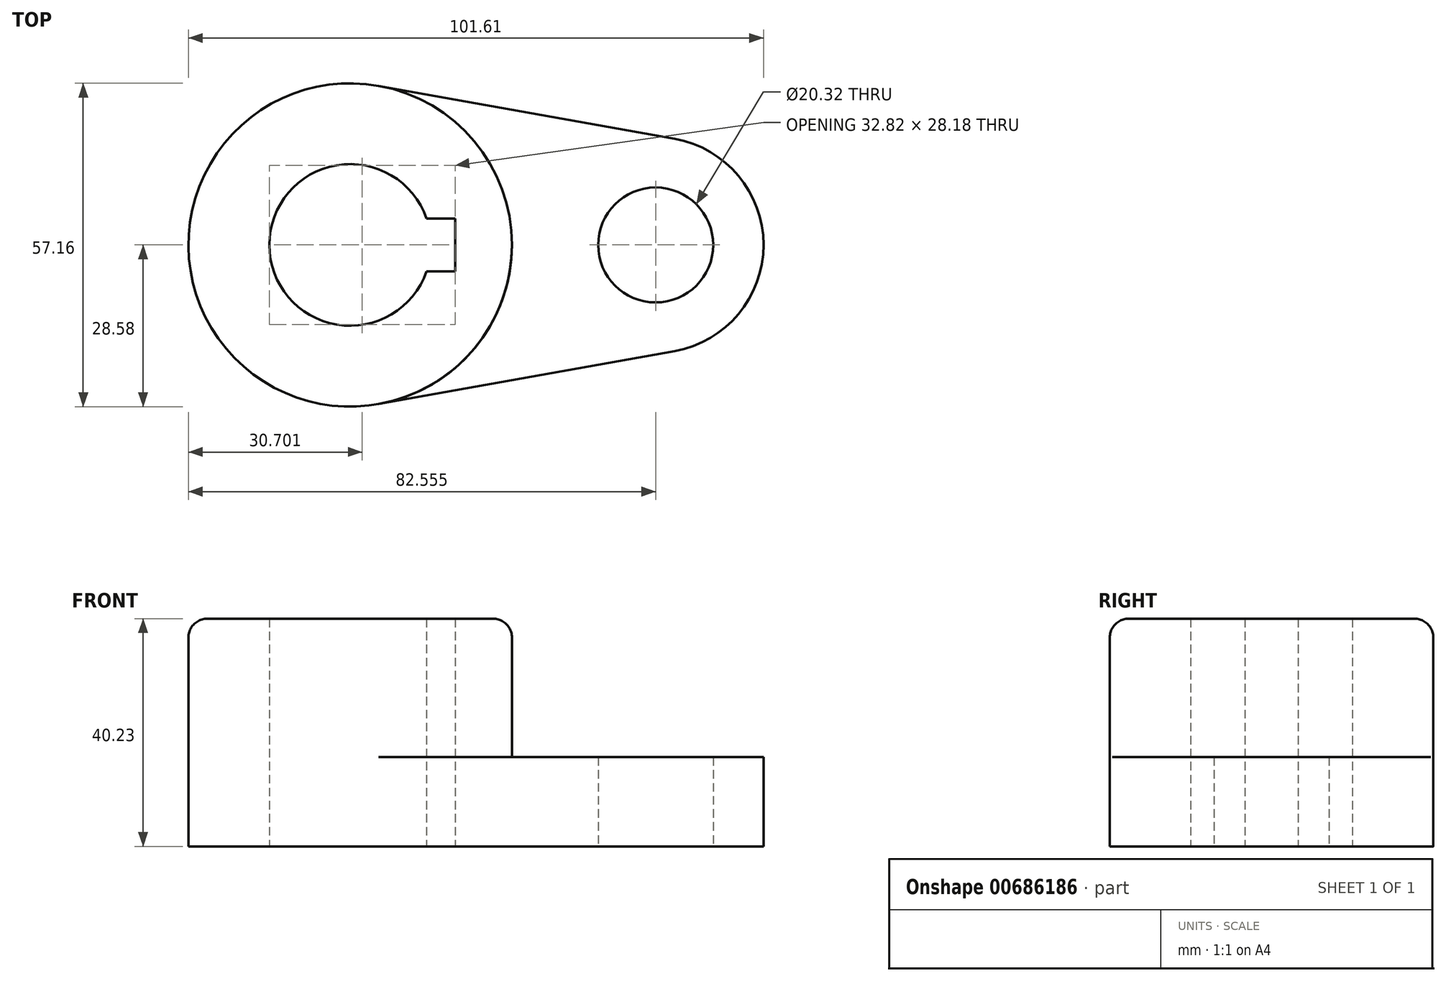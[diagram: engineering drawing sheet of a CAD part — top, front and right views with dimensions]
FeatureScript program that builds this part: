
annotation { "Feature Type Name" : "Feature", "Feature Type Description" : "" }
export const myFeature = defineFeature(function(context is Context, id is Id, definition is map)
    precondition{}
    {
        {
            var Q0;
            Q0=qCreatedBy(makeId("Top.planeOp"),FACE);
            var sketch = newSketch(context, id + "F0", { "sketchPlane" : qUnion([Q0])});
            skCircle(sketch, "E0", {"center": v(0, 0) * mm, "radius": 28.58 * mm});
            skPoint(sketch, "E1.orphan", {"position": v(-12.82, 3.46) * mm});
            skPoint(sketch, "E2.orphan", {"position": v(-12.82, -3.46) * mm});
            skCircle(sketch, "E3", {"center": v(53.98, 0) * mm, "radius": 19.05 * mm});
            skArc(sketch, "E4", {"start": v(13.5, 4.69) * mm, "mid": v(-14.29, 0) * mm, "end": v(13.5, -4.69) * mm});
            skPoint(sketch, "E5.left.end.orphan", {"position": v(12.82, 3.46) * mm});
            skPoint(sketch, "E5.bottom.start.orphan", {"position": v(12.82, -3.46) * mm});
            skLineSegment(sketch, "E6.bottom", {"start": v(13.5, 4.69) * mm, "end": v(18.53, 4.69) * mm});
            skLineSegment(sketch, "E6.top", {"start": v(13.5, -4.69) * mm, "end": v(18.53, -4.69) * mm});
            skLineSegment(sketch, "E6.right", {"start": v(18.53, 4.69) * mm, "end": v(18.53, -4.69) * mm});
            skPoint(sketch, "E6.left.start.orphan", {"position": v(-18.53, 4.69) * mm});
            skPoint(sketch, "E7.orphan", {"position": v(-18.53, -4.69) * mm});
            skLineSegment(sketch, "E8", {"start": v(5.04, 28.13) * mm, "end": v(57.34, 18.75) * mm});
            skLineSegment(sketch, "E9", {"start": v(5.04, -28.13) * mm, "end": v(57.34, -18.75) * mm});
            skCircle(sketch, "E10", {"center": v(53.98, 0) * mm, "radius": 10.16 * mm});
            skSolve(sketch);
        }
        {
            var Q0;
            Q0=makeQuery(id+"F0.imprint","IMPRINT",FACE,{"disambiguationData":[TD([[makeQuery(id+"F0.imprint","IMPRINT",EDGE,{"derivedFrom":sQuery(id+"F0.wireOp",EDGE,"E4")}),-1.0]])]});
            extrude(context, id + "F1", {"entities" : qUnion([Q0]), "depth" : 40.23 * mm, "offsetDistance" : 25.4 * mm});
        }
        {
            var Q0;
            Q0 = qSketchRegion(id + "F0", true);
            extrude(context, id + "F2", {"entities" : qUnion([Q0]), "operationType" : NewBodyOperationType.ADD, "depth" : 15.77 * mm, "offsetDistance" : 25.4 * mm});
        }
        {
            var Q0;
            Q0=makeQuery(id+"F1.opExtrude","CAP_EDGE",EDGE,{"disambiguationData":[OSD([sQuery(id+"F0.wireOp",EDGE,"E0")])],"isStart":false});
            fillet(context, id + "F3", {"entities" : qUnion([Q0]), "radius" : 3.3 * mm, "tangentPropagation" : true, "allowEdgeOverflow" : false});
        }
    });
